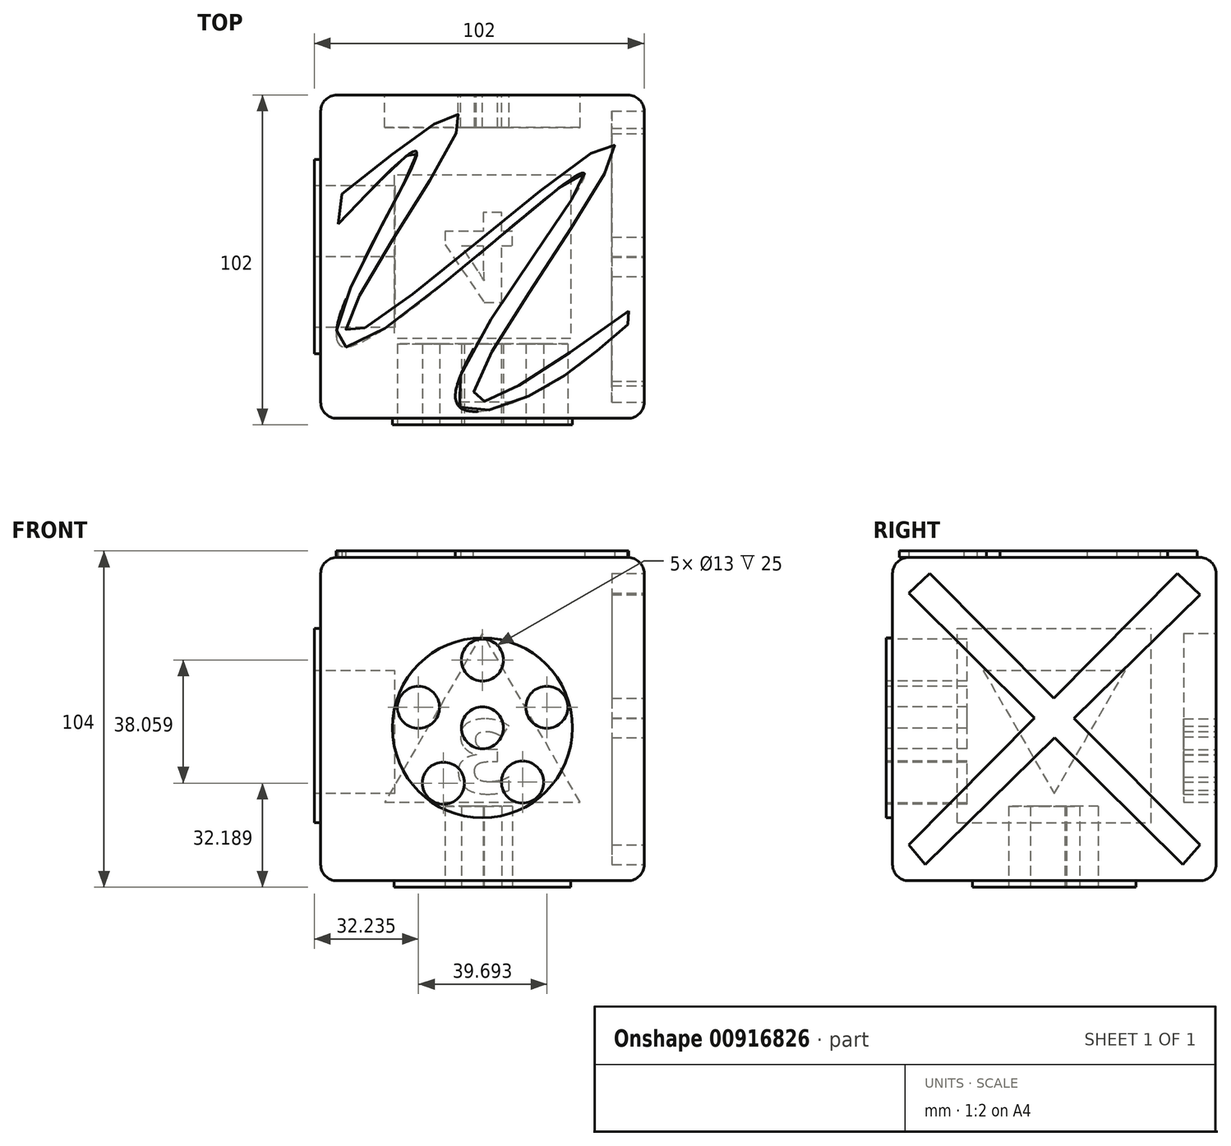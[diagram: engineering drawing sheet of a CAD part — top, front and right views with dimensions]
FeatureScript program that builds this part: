
annotation { "Feature Type Name" : "Feature", "Feature Type Description" : "" }
export const myFeature = defineFeature(function(context is Context, id is Id, definition is map)
    precondition{}
    {
        {
            var Q0;
            Q0=qCreatedBy(makeId("Top.planeOp"),FACE);
            var sketch = newSketch(context, id + "F0", { "sketchPlane" : qUnion([Q0])});
            skLineSegment(sketch, "E0.bottom", {"start": v(50, -50) * mm, "end": v(-50, -50) * mm});
            skLineSegment(sketch, "E0.top", {"start": v(50, 50) * mm, "end": v(-50, 50) * mm});
            skLineSegment(sketch, "E0.left", {"start": v(50, -50) * mm, "end": v(50, 50) * mm});
            skLineSegment(sketch, "E0.right", {"start": v(-50, -50) * mm, "end": v(-50, 50) * mm});
            skPoint(sketch, "E0.middle", {"position": v(0, 0) * mm});
            skSolve(sketch);
        }
        {
            var Q0;
            Q0=makeQuery(id+"F0.imprint","IMPRINT",FACE,{"disambiguationData":[TD([[makeQuery(id+"F0.imprint","IMPRINT",EDGE,{"derivedFrom":sQuery(id+"F0.wireOp",EDGE,"E0.bottom")}),-1.0]])]});
            extrude(context, id + "F1", {"entities" : qUnion([Q0]), "depth" : 100 * mm, "offsetDistance" : 25 * mm});
        }
        {
            var Q0;
            Q0=makeQuery(id+"F1.opExtrude","SWEPT_EDGE",EDGE,{"disambiguationData":[OSD([sQuery(id+"F0.wireOp",EDGE,"E0.bottom"),sQuery(id+"F0.wireOp",EDGE,"E0.left")])]});
            var Q1;
            Q1=makeQuery(id+"F1.opExtrude","SWEPT_EDGE",EDGE,{"disambiguationData":[OSD([sQuery(id+"F0.wireOp",EDGE,"E0.bottom"),sQuery(id+"F0.wireOp",EDGE,"E0.right")])]});
            var Q2;
            Q2=makeQuery(id+"F1.opExtrude","SWEPT_EDGE",EDGE,{"disambiguationData":[OSD([sQuery(id+"F0.wireOp",EDGE,"E0.top"),sQuery(id+"F0.wireOp",EDGE,"E0.left")])]});
            var Q3;
            Q3=makeQuery(id+"F1.opExtrude","CAP_EDGE",EDGE,{"disambiguationData":[OSD([sQuery(id+"F0.wireOp",EDGE,"E0.bottom")])],"isStart":true});
            var Q4;
            Q4=makeQuery(id+"F1.opExtrude","CAP_EDGE",EDGE,{"disambiguationData":[OSD([sQuery(id+"F0.wireOp",EDGE,"E0.bottom")])],"isStart":false});
            var Q5;
            Q5=makeQuery(id+"F1.opExtrude","CAP_EDGE",EDGE,{"disambiguationData":[OSD([sQuery(id+"F0.wireOp",EDGE,"E0.left")])],"isStart":true});
            var Q6;
            Q6=makeQuery(id+"F1.opExtrude","CAP_EDGE",EDGE,{"disambiguationData":[OSD([sQuery(id+"F0.wireOp",EDGE,"E0.left")])],"isStart":false});
            var Q7;
            Q7=makeQuery(id+"F1.opExtrude","CAP_EDGE",EDGE,{"disambiguationData":[OSD([sQuery(id+"F0.wireOp",EDGE,"E0.top")])],"isStart":true});
            var Q8;
            Q8=makeQuery(id+"F1.opExtrude","CAP_EDGE",EDGE,{"disambiguationData":[OSD([sQuery(id+"F0.wireOp",EDGE,"E0.right")])],"isStart":true});
            var Q9;
            Q9=makeQuery(id+"F1.opExtrude","SWEPT_EDGE",EDGE,{"disambiguationData":[OSD([sQuery(id+"F0.wireOp",EDGE,"E0.top"),sQuery(id+"F0.wireOp",EDGE,"E0.right")])]});
            var Q10;
            Q10=makeQuery(id+"F1.opExtrude","CAP_EDGE",EDGE,{"disambiguationData":[OSD([sQuery(id+"F0.wireOp",EDGE,"E0.top")])],"isStart":false});
            var Q11;
            Q11=makeQuery(id+"F1.opExtrude","CAP_EDGE",EDGE,{"disambiguationData":[OSD([sQuery(id+"F0.wireOp",EDGE,"E0.right")])],"isStart":false});
            fillet(context, id + "F2", {"entities" : qUnion([Q0, Q1, Q2, Q3, Q4, Q5, Q6, Q7, Q8, Q9, Q10, Q11]), "radius" : 5 * mm, "tangentPropagation" : true, "allowEdgeOverflow" : false});
        }
        {
            var Q0;
            Q0=makeQuery(id+"F1.opExtrude","SWEPT_FACE",FACE,{"disambiguationData":[OSD([sQuery(id+"F0.wireOp",EDGE,"E0.bottom")])]});
            var sketch = newSketch(context, id + "F3", { "sketchPlane" : qUnion([Q0])});
            skCircle(sketch, "E1", {"center": v(0, 47.3) * mm, "radius": 27.85 * mm});
            skSolve(sketch);
        }
        {
            var Q0;
            Q0=makeQuery(id+"F3.imprint","IMPRINT",FACE,{"disambiguationData":[TD([[makeQuery(id+"F3.imprint","IMPRINT",EDGE,{"derivedFrom":sQuery(id+"F3.wireOp",EDGE,"E1")}),1.0]])]});
            extrude(context, id + "F4", {"entities" : qUnion([Q0]), "operationType" : NewBodyOperationType.ADD, "depth" : 2 * mm, "offsetDistance" : 25 * mm});
        }
        {
            var Q0;
            Q0=makeQuery(id+"F4.opExtrude","CAP_FACE",FACE,{"disambiguationData":[OSD([sQuery(id+"F3.wireOp",EDGE,"E1")])],"isStart":false});
            var sketch = newSketch(context, id + "F5", { "sketchPlane" : qUnion([Q0])});
            skPoint(sketch, "E2.0.midPoint", {"position": v(0, 31.25) * mm});
            skCircle(sketch, "E3", {"center": v(-19.76, 53.61) * mm, "radius": 6.5 * mm});
            skCircle(sketch, "E4", {"center": v(0, 68.25) * mm, "radius": 6.5 * mm});
            skCircle(sketch, "E5", {"center": v(19.93, 53.66) * mm, "radius": 6.5 * mm});
            skCircle(sketch, "E6", {"center": v(-12.05, 30.19) * mm, "radius": 6.5 * mm});
            skCircle(sketch, "E7", {"center": v(12.4, 30.51) * mm, "radius": 6.5 * mm});
            skCircle(sketch, "E8", {"center": v(0, 47.3) * mm, "radius": 6.49 * mm});
            skSolve(sketch);
        }
        {
            var Q0;
            Q0=makeQuery(id+"F5.imprint","IMPRINT",FACE,{"disambiguationData":[TD([[makeQuery(id+"F5.imprint","IMPRINT",EDGE,{"derivedFrom":sQuery(id+"F5.wireOp",EDGE,"E3")}),1.0]])]});
            var Q1;
            Q1=makeQuery(id+"F5.imprint","IMPRINT",FACE,{"disambiguationData":[TD([[makeQuery(id+"F5.imprint","IMPRINT",EDGE,{"derivedFrom":sQuery(id+"F5.wireOp",EDGE,"E5")}),1.0]])]});
            var Q2;
            Q2=makeQuery(id+"F5.imprint","IMPRINT",FACE,{"disambiguationData":[TD([[makeQuery(id+"F5.imprint","IMPRINT",EDGE,{"derivedFrom":sQuery(id+"F5.wireOp",EDGE,"E6")}),1.0]])]});
            var Q3;
            Q3=makeQuery(id+"F5.imprint","IMPRINT",FACE,{"disambiguationData":[TD([[makeQuery(id+"F5.imprint","IMPRINT",EDGE,{"derivedFrom":sQuery(id+"F5.wireOp",EDGE,"E7")}),1.0]])]});
            var Q4;
            Q4=makeQuery(id+"F5.imprint","IMPRINT",FACE,{"disambiguationData":[TD([[makeQuery(id+"F5.imprint","IMPRINT",EDGE,{"derivedFrom":sQuery(id+"F5.wireOp",EDGE,"E8")}),1.0]])]});
            var Q5;
            Q5=makeQuery(id+"F5.imprint","IMPRINT",FACE,{"disambiguationData":[TD([[makeQuery(id+"F5.imprint","IMPRINT",EDGE,{"derivedFrom":sQuery(id+"F5.wireOp",EDGE,"E4")}),1.0]])]});
            extrude(context, id + "F6", {"entities" : qUnion([Q0, Q1, Q2, Q3, Q4, Q5]), "operationType" : NewBodyOperationType.REMOVE, "oppositeDirection" : true, "depth" : 25 * mm, "offsetDistance" : 25 * mm});
        }
        {
            var Q0;
            Q0=makeQuery(id+"F1.opExtrude","SWEPT_FACE",FACE,{"disambiguationData":[OSD([sQuery(id+"F0.wireOp",EDGE,"E0.right")])]});
            var sketch = newSketch(context, id + "F7", { "sketchPlane" : qUnion([Q0])});
            skSolve(sketch);
        }
        {
            var Q0;
            {var subQ0=sQuery(id+"F0.wireOp",EDGE,"E0.right");var subQ1=makeQuery(id+"F1.opExtrude","SWEPT_FACE",FACE,{"disambiguationData":[OSD([subQ0])]});Q0=makeQuery(id+"F7.imprint","IMPRINT",FACE,{"disambiguationData":[TD([[makeQuery(id+"F7.imprint","IMPRINT",EDGE,{"derivedFrom":makeQuery(id+"F2.opFillet","BLEND_EDGE",EDGE,{"blendedFrom":[makeQuery(id+"F1.opExtrude","CAP_EDGE",EDGE,{"disambiguationData":[OSD([subQ0])],"isStart":true}),subQ1],"blendedInto":[subQ1]})}),1.0]])]});}
            var sketch = newSketch(context, id + "F8", { "sketchPlane" : qUnion([Q0])});
            skLineSegment(sketch, "E9.bottom", {"start": v(30, 18) * mm, "end": v(-30, 18) * mm});
            skLineSegment(sketch, "E9.top", {"start": v(30, 78) * mm, "end": v(-30, 78) * mm});
            skLineSegment(sketch, "E9.left", {"start": v(30, 18) * mm, "end": v(30, 78) * mm});
            skLineSegment(sketch, "E9.right", {"start": v(-30, 18) * mm, "end": v(-30, 78) * mm});
            skPoint(sketch, "E9.middle", {"position": v(0, 48) * mm});
            skSolve(sketch);
        }
        {
            var Q0;
            Q0=makeQuery(id+"F8.imprint","IMPRINT",FACE,{"disambiguationData":[TD([[makeQuery(id+"F8.imprint","IMPRINT",EDGE,{"derivedFrom":sQuery(id+"F8.wireOp",EDGE,"E9.bottom")}),-1.0]])]});
            extrude(context, id + "F9", {"entities" : qUnion([Q0]), "operationType" : NewBodyOperationType.ADD, "depth" : 2 * mm, "offsetDistance" : 25 * mm});
        }
        {
            var Q0;
            Q0=makeQuery(id+"F9.opExtrude","CAP_FACE",FACE,{"disambiguationData":[OSD([sQuery(id+"F8.wireOp",EDGE,"E9.bottom"),sQuery(id+"F8.wireOp",EDGE,"E9.top"),sQuery(id+"F8.wireOp",EDGE,"E9.left"),sQuery(id+"F8.wireOp",EDGE,"E9.right")])],"isStart":false});
            var sketch = newSketch(context, id + "F10", { "sketchPlane" : qUnion([Q0])});
            skCircle(sketch, "E10.cCircle", {"center": v(0, 52.28) * mm, "radius": 12.67 * mm, "construction": true});
            skLineSegment(sketch, "E10.0", {"start": v(-21.94, 64.95) * mm, "end": v(21.94, 64.95) * mm});
            skLineSegment(sketch, "E10.1", {"start": v(21.94, 64.95) * mm, "end": v(0, 26.95) * mm});
            skLineSegment(sketch, "E10.2", {"start": v(0, 26.95) * mm, "end": v(-21.94, 64.95) * mm});
            skPoint(sketch, "E10.0.midPoint", {"position": v(0, 64.95) * mm});
            skSolve(sketch);
        }
        {
            var Q0;
            Q0=makeQuery(id+"F10.imprint","IMPRINT",FACE,{"disambiguationData":[TD([[makeQuery(id+"F10.imprint","IMPRINT",EDGE,{"derivedFrom":sQuery(id+"F10.wireOp",EDGE,"E10.0")}),-1.0]])]});
            extrude(context, id + "F11", {"entities" : qUnion([Q0]), "operationType" : NewBodyOperationType.REMOVE, "oppositeDirection" : true, "depth" : 25 * mm, "offsetDistance" : 25 * mm});
        }
        {
            var Q0;
            Q0=makeQuery(id+"F1.opExtrude","CAP_FACE",FACE,{"disambiguationData":[OSD([sQuery(id+"F0.wireOp",EDGE,"E0.bottom"),sQuery(id+"F0.wireOp",EDGE,"E0.top"),sQuery(id+"F0.wireOp",EDGE,"E0.left"),sQuery(id+"F0.wireOp",EDGE,"E0.right")])],"isStart":false});
            var sketch = newSketch(context, id + "F12", { "sketchPlane" : qUnion([Q0])});
            skSolve(sketch);
        }
        {
            var Q0;
            {var subQ0=sQuery(id+"F0.wireOp",EDGE,"E0.right");var subQ1=sQuery(id+"F0.wireOp",EDGE,"E0.left");var subQ2=sQuery(id+"F0.wireOp",EDGE,"E0.top");var subQ3=sQuery(id+"F0.wireOp",EDGE,"E0.bottom");var subQ4=makeQuery(id+"F1.opExtrude","CAP_FACE",FACE,{"disambiguationData":[OSD([subQ3,subQ2,subQ1,subQ0])],"isStart":false});Q0=makeQuery(id+"F12.imprint","IMPRINT",FACE,{"disambiguationData":[TD([[makeQuery(id+"F12.imprint","IMPRINT",EDGE,{"derivedFrom":makeQuery(id+"F2.opFillet","BLEND_EDGE",EDGE,{"blendedFrom":[makeQuery(id+"F1.opExtrude","CAP_EDGE",EDGE,{"disambiguationData":[OSD([subQ3])],"isStart":false}),subQ4],"blendedInto":[subQ4]})}),1.0]])]});}
            var sketch = newSketch(context, id + "F13", { "sketchPlane" : qUnion([Q0])});
            skFitSpline(sketch, "E11", {"points": [v(-43.38, 19.34) * mm, v(-6.75, 41.78) * mm, v(-41.55, -23.7) * mm, v(40.4, 34.91) * mm, v(-2.63, -41.55) * mm, v(45.21, -16.83) * mm], "startDerivative": vector(368.46, 295.24) * mm, "endDerivative": vector(427.79, 304.33) * mm});
            skFitSpline(sketch, "E12", {"points": [v(-44.53, 10.19) * mm, v(-20.26, 32.16) * mm, v(-44.53, -19.8) * mm, v(-40.18, -27.59) * mm, v(31.48, 25.75) * mm, v(-8.36, -43.15) * mm, v(11.56, -44.3) * mm, v(44.98, -20.95) * mm], "startDerivative": vector(287.43, 301.98) * mm, "endDerivative": vector(216.6, 190.73) * mm});
            skFitSpline(sketch, "E13", {"points": [v(130.83, -33.54) * mm, v(121.22, -31.93) * mm], "startDerivative": vector(-9.61, 1.6) * mm, "endDerivative": vector(-9.61, 1.6) * mm});
            skLineSegment(sketch, "E14", {"start": v(-43.38, 19.34) * mm, "end": v(-44.53, 10.19) * mm});
            skLineSegment(sketch, "E15", {"start": v(45.21, -16.83) * mm, "end": v(44.98, -20.95) * mm});
            skLineSegment(sketch, "E16", {"start": v(128.54, -9.04) * mm, "end": v(126.25, -9.04) * mm});
            skLineSegment(sketch, "E17", {"start": v(126.25, -9.04) * mm, "end": v(126.25, -4.92) * mm});
            skLineSegment(sketch, "E18", {"start": v(126.25, -4.92) * mm, "end": v(124.65, -4.92) * mm});
            skSolve(sketch);
        }
        {
            var Q0;
            Q0 = qSketchRegion(id + "F13", true);
            extrude(context, id + "F14", {"entities" : qUnion([Q0]), "operationType" : NewBodyOperationType.ADD, "depth" : 2 * mm, "offsetDistance" : 25 * mm});
        }
        {
            var Q0;
            Q0=makeQuery(id+"F1.opExtrude","SWEPT_FACE",FACE,{"disambiguationData":[OSD([sQuery(id+"F0.wireOp",EDGE,"E0.top")])]});
            var sketch = newSketch(context, id + "F15", { "sketchPlane" : qUnion([Q0])});
            skCircle(sketch, "E19.cCircle", {"center": v(0, 41.7) * mm, "radius": 17.43 * mm, "construction": true});
            skLineSegment(sketch, "E19.0", {"start": v(30.2, 24.26) * mm, "end": v(-30.2, 24.26) * mm});
            skLineSegment(sketch, "E19.1", {"start": v(-30.2, 24.26) * mm, "end": v(0, 76.57) * mm});
            skLineSegment(sketch, "E19.2", {"start": v(0, 76.57) * mm, "end": v(30.2, 24.26) * mm});
            skPoint(sketch, "E19.0.midPoint", {"position": v(0, 24.26) * mm});
            skText(sketch, "E20", { "text": "3", "fontName": "OpenSans-Bold.ttf"});
            const initialGuessF15  = {"E20": [-0.00946, 0.02708, 1, 0, 0.02287]};
            skSetInitialGuess(sketch, initialGuessF15);
            skSolve(sketch);
        }
        {
            var Q0;
            Q0=makeQuery(id+"F15.imprint","IMPRINT",FACE,{"disambiguationData":[TD([[makeQuery(id+"F15.imprint","IMPRINT",EDGE,{"derivedFrom":sQuery(id+"F15.wireOp",EDGE,"E19.0")}),-1.0]])]});
            extrude(context, id + "F16", {"entities" : qUnion([Q0]), "operationType" : NewBodyOperationType.REMOVE, "oppositeDirection" : true, "depth" : 10 * mm, "offsetDistance" : 25 * mm});
        }
        {
            var Q0;
            Q0=makeQuery(id+"F1.opExtrude","SWEPT_FACE",FACE,{"disambiguationData":[OSD([sQuery(id+"F0.wireOp",EDGE,"E0.left")])]});
            var sketch = newSketch(context, id + "F17", { "sketchPlane" : qUnion([Q0])});
            skLineSegment(sketch, "E21", {"start": v(-38.53, 95) * mm, "end": v(45, 11.07) * mm});
            skLineSegment(sketch, "E22", {"start": v(-45, 88.9) * mm, "end": v(39.77, 5) * mm});
            skLineSegment(sketch, "E23", {"start": v(38.06, 95) * mm, "end": v(-45, 11.07) * mm});
            skLineSegment(sketch, "E24", {"start": v(45, 88.44) * mm, "end": v(-39.93, 5) * mm});
            skLineSegment(sketch, "E25", {"start": v(-45, 11.07) * mm, "end": v(-39.93, 5) * mm});
            skLineSegment(sketch, "E26", {"start": v(-38.53, 95) * mm, "end": v(-45, 88.9) * mm});
            skLineSegment(sketch, "E27", {"start": v(45, 11.07) * mm, "end": v(39.77, 5) * mm});
            skLineSegment(sketch, "E28", {"start": v(38.06, 95) * mm, "end": v(45, 88.44) * mm});
            skSolve(sketch);
        }
        {
            var Q0;
            {var subQ0=sQuery(id+"F17.wireOp",EDGE,"E23");var subQ1=sQuery(id+"F17.wireOp",EDGE,"E21");var subQ2=makeQuery(id+"F17.imprint","INTERSECT",VERTEX,{"derivedFrom":[subQ1,subQ0]});Q0=makeQuery(id+"F17.imprint","IMPRINT",FACE,{"disambiguationData":[TD([[makeQuery(id+"F17.imprint","IMPRINT",EDGE,{"disambiguationData":[TD([[subQ2,-1.0]])],"derivedFrom":subQ1}),-1.0]])]});}
            var Q1;
            {var subQ5=sQuery(id+"F17.wireOp",EDGE,"E28");Q1=makeQuery(id+"F17.imprint","IMPRINT",FACE,{"disambiguationData":[TD([[makeQuery(id+"F17.imprint","IMPRINT",EDGE,{"derivedFrom":subQ5}),-1.0]])]});}
            var Q2;
            {var subQ0=sQuery(id+"F17.wireOp",EDGE,"E27");Q2=makeQuery(id+"F17.imprint","IMPRINT",FACE,{"disambiguationData":[TD([[makeQuery(id+"F17.imprint","IMPRINT",EDGE,{"derivedFrom":subQ0}),-1.0]])]});}
            var Q3;
            {var subQ5=sQuery(id+"F17.wireOp",EDGE,"E25");Q3=makeQuery(id+"F17.imprint","IMPRINT",FACE,{"disambiguationData":[TD([[makeQuery(id+"F17.imprint","IMPRINT",EDGE,{"derivedFrom":subQ5}),1.0]])]});}
            var Q4;
            {var subQ0=sQuery(id+"F17.wireOp",EDGE,"E26");Q4=makeQuery(id+"F17.imprint","IMPRINT",FACE,{"disambiguationData":[TD([[makeQuery(id+"F17.imprint","IMPRINT",EDGE,{"derivedFrom":subQ0}),1.0]])]});}
            extrude(context, id + "F18", {"entities" : qUnion([Q0, Q1, Q2, Q3, Q4]), "operationType" : NewBodyOperationType.REMOVE, "oppositeDirection" : true, "depth" : 10 * mm, "offsetDistance" : 25 * mm});
        }
        {
            var Q0;
            Q0=makeQuery(id+"F1.opExtrude","CAP_FACE",FACE,{"disambiguationData":[OSD([sQuery(id+"F0.wireOp",EDGE,"E0.bottom"),sQuery(id+"F0.wireOp",EDGE,"E0.top"),sQuery(id+"F0.wireOp",EDGE,"E0.left"),sQuery(id+"F0.wireOp",EDGE,"E0.right")])],"isStart":true});
            var sketch = newSketch(context, id + "F19", { "sketchPlane" : qUnion([Q0])});
            skLineSegment(sketch, "E29.bottom", {"start": v(27.36, -25.3) * mm, "end": v(-27.36, -25.3) * mm});
            skLineSegment(sketch, "E29.top", {"start": v(27.36, 25.3) * mm, "end": v(-27.36, 25.3) * mm});
            skLineSegment(sketch, "E29.left", {"start": v(27.36, -25.3) * mm, "end": v(27.36, 25.3) * mm});
            skLineSegment(sketch, "E29.right", {"start": v(-27.36, -25.3) * mm, "end": v(-27.36, 25.3) * mm});
            skPoint(sketch, "E29.middle", {"position": v(0, 0) * mm});
            skSolve(sketch);
        }
        {
            var Q0;
            Q0 = qSketchRegion(id + "F19", true);
            extrude(context, id + "F20", {"entities" : qUnion([Q0]), "operationType" : NewBodyOperationType.ADD, "depth" : 2 * mm, "offsetDistance" : 25 * mm});
        }
        {
            var Q0;
            Q0=makeQuery(id+"F20.opExtrude","CAP_FACE",FACE,{"disambiguationData":[OSD([sQuery(id+"F19.wireOp",EDGE,"E29.bottom"),sQuery(id+"F19.wireOp",EDGE,"E29.top"),sQuery(id+"F19.wireOp",EDGE,"E29.left"),sQuery(id+"F19.wireOp",EDGE,"E29.right")])],"isStart":false});
            var sketch = newSketch(context, id + "F21", { "sketchPlane" : qUnion([Q0])});
            skText(sketch, "E30", { "text": "4\n", "fontName": "OpenSans-Bold.ttf"});
            const initialGuessF21  = {"E30": [-0.01225, -0.01362, 1, 0, 0.02793]};
            skSetInitialGuess(sketch, initialGuessF21);
            skSolve(sketch);
        }
        {
            var Q0;
            Q0 = qSketchRegion(id + "F21", true);
            extrude(context, id + "F22", {"entities" : qUnion([Q0]), "operationType" : NewBodyOperationType.REMOVE, "oppositeDirection" : true, "depth" : 25 * mm, "offsetDistance" : 25 * mm});
        }
    });
